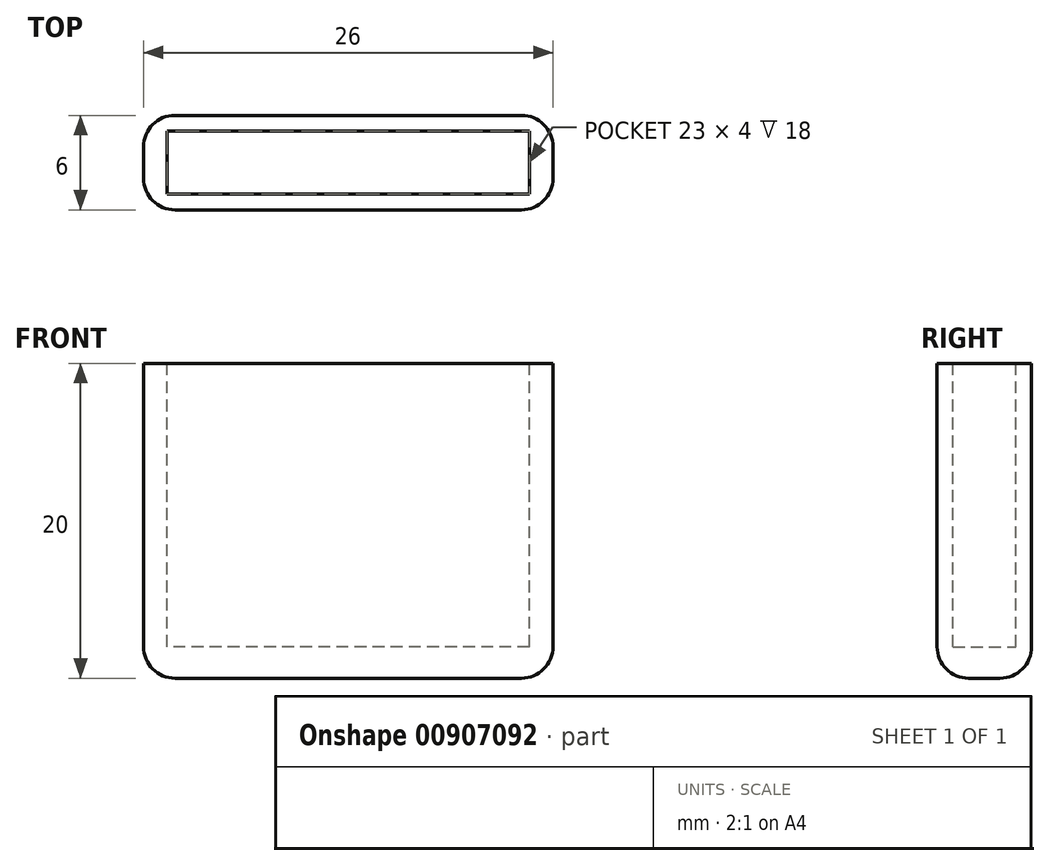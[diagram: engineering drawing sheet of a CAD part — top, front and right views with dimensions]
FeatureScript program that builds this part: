
annotation { "Feature Type Name" : "Feature", "Feature Type Description" : "" }
export const myFeature = defineFeature(function(context is Context, id is Id, definition is map)
    precondition{}
    {
        {
            var Q0;
            Q0=qCreatedBy(makeId("Top.planeOp"),FACE);
            var sketch = newSketch(context, id + "F0", { "sketchPlane" : qUnion([Q0])});
            skLineSegment(sketch, "E0.bottom", {"start": v(13, -3) * mm, "end": v(-13, -3) * mm});
            skLineSegment(sketch, "E0.top", {"start": v(13, 3) * mm, "end": v(-13, 3) * mm});
            skLineSegment(sketch, "E0.left", {"start": v(13, -3) * mm, "end": v(13, 3) * mm});
            skLineSegment(sketch, "E0.right", {"start": v(-13, -3) * mm, "end": v(-13, 3) * mm});
            skPoint(sketch, "E0.middle", {"position": v(0, 0) * mm});
            skSolve(sketch);
        }
        {
            var Q0;
            Q0=makeQuery(id+"F0.imprint","IMPRINT",FACE,{"disambiguationData":[TD([[makeQuery(id+"F0.imprint","IMPRINT",EDGE,{"derivedFrom":sQuery(id+"F0.wireOp",EDGE,"E0.bottom")}),-1.0]])]});
            extrude(context, id + "F1", {"entities" : qUnion([Q0]), "depth" : 20 * mm, "offsetDistance" : 25 * mm});
        }
        {
            var Q0;
            Q0=makeQuery(id+"F1.opExtrude","CAP_FACE",FACE,{"disambiguationData":[OSD([sQuery(id+"F0.wireOp",EDGE,"E0.bottom"),sQuery(id+"F0.wireOp",EDGE,"E0.top"),sQuery(id+"F0.wireOp",EDGE,"E0.left"),sQuery(id+"F0.wireOp",EDGE,"E0.right")])],"isStart":false});
            var sketch = newSketch(context, id + "F2", { "sketchPlane" : qUnion([Q0])});
            skLineSegment(sketch, "E1.bottom", {"start": v(11.5, -2) * mm, "end": v(-11.5, -2) * mm});
            skLineSegment(sketch, "E1.top", {"start": v(11.5, 2) * mm, "end": v(-11.5, 2) * mm});
            skLineSegment(sketch, "E1.left", {"start": v(11.5, -2) * mm, "end": v(11.5, 2) * mm});
            skLineSegment(sketch, "E1.right", {"start": v(-11.5, -2) * mm, "end": v(-11.5, 2) * mm});
            skPoint(sketch, "E1.middle", {"position": v(0, 0) * mm});
            skSolve(sketch);
        }
        {
            var Q0;
            Q0=makeQuery(id+"F2.imprint","IMPRINT",FACE,{"disambiguationData":[TD([[makeQuery(id+"F2.imprint","IMPRINT",EDGE,{"derivedFrom":sQuery(id+"F2.wireOp",EDGE,"E1.bottom")}),-1.0]])]});
            extrude(context, id + "F3", {"entities" : qUnion([Q0]), "operationType" : NewBodyOperationType.REMOVE, "oppositeDirection" : true, "depth" : 18 * mm, "offsetDistance" : 25 * mm});
        }
        {
            var Q0;
            Q0=makeQuery(id+"F1.opExtrude","SWEPT_EDGE",EDGE,{"disambiguationData":[OSD([sQuery(id+"F0.wireOp",EDGE,"E0.top"),sQuery(id+"F0.wireOp",EDGE,"E0.right")])]});
            var Q1;
            Q1=makeQuery(id+"F1.opExtrude","SWEPT_EDGE",EDGE,{"disambiguationData":[OSD([sQuery(id+"F0.wireOp",EDGE,"E0.bottom"),sQuery(id+"F0.wireOp",EDGE,"E0.right")])]});
            var Q2;
            Q2=makeQuery(id+"F1.opExtrude","CAP_FACE",FACE,{"disambiguationData":[OSD([sQuery(id+"F0.wireOp",EDGE,"E0.bottom"),sQuery(id+"F0.wireOp",EDGE,"E0.top"),sQuery(id+"F0.wireOp",EDGE,"E0.left"),sQuery(id+"F0.wireOp",EDGE,"E0.right")])],"isStart":true});
            var Q3;
            Q3=makeQuery(id+"F1.opExtrude","SWEPT_EDGE",EDGE,{"disambiguationData":[OSD([sQuery(id+"F0.wireOp",EDGE,"E0.bottom"),sQuery(id+"F0.wireOp",EDGE,"E0.left")])]});
            var Q4;
            Q4=makeQuery(id+"F1.opExtrude","SWEPT_EDGE",EDGE,{"disambiguationData":[OSD([sQuery(id+"F0.wireOp",EDGE,"E0.top"),sQuery(id+"F0.wireOp",EDGE,"E0.left")])]});
            fillet(context, id + "F4", {"entities" : qUnion([Q0, Q1, Q2, Q3, Q4]), "radius" : 2 * mm, "tangentPropagation" : true, "allowEdgeOverflow" : false});
        }
    });
